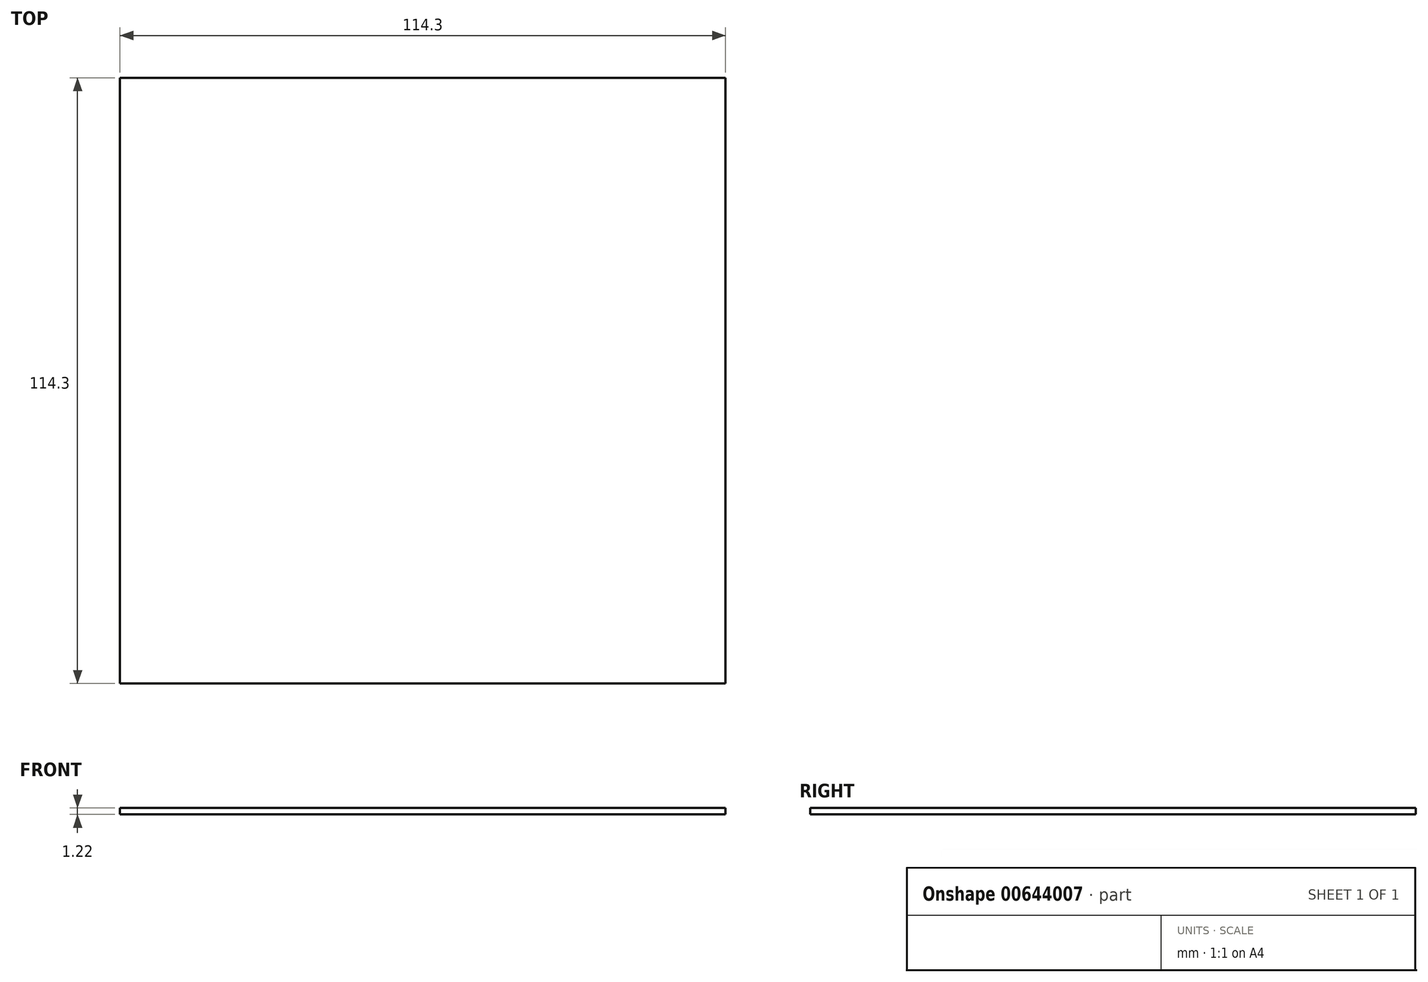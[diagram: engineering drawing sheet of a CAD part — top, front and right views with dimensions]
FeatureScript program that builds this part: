
annotation { "Feature Type Name" : "Feature", "Feature Type Description" : "" }
export const myFeature = defineFeature(function(context is Context, id is Id, definition is map)
    precondition{}
    {
        {
            var Q0;
            Q0=qCreatedBy(makeId("Top.planeOp"),FACE);
            var sketch = newSketch(context, id + "F0", { "sketchPlane" : qUnion([Q0])});
            skLineSegment(sketch, "E0.bottom", {"start": v(-71.56, -79.62) * mm, "end": v(42.74, -79.62) * mm});
            skLineSegment(sketch, "E0.top", {"start": v(-71.56, 34.68) * mm, "end": v(42.74, 34.68) * mm});
            skLineSegment(sketch, "E0.left", {"start": v(-71.56, -79.62) * mm, "end": v(-71.56, 34.68) * mm});
            skLineSegment(sketch, "E0.right", {"start": v(42.74, -79.62) * mm, "end": v(42.74, 34.68) * mm});
            skSolve(sketch);
        }
        {
            var Q0;
            Q0=makeQuery(id+"F0.imprint","IMPRINT",FACE,{"disambiguationData":[TD([[makeQuery(id+"F0.imprint","IMPRINT",EDGE,{"derivedFrom":sQuery(id+"F0.wireOp",EDGE,"E0.bottom")}),1.0]])]});
            extrude(context, id + "F1", {"entities" : qUnion([Q0]), "depth" : 1.22 * mm, "offsetDistance" : 25.4 * mm});
        }
    });
